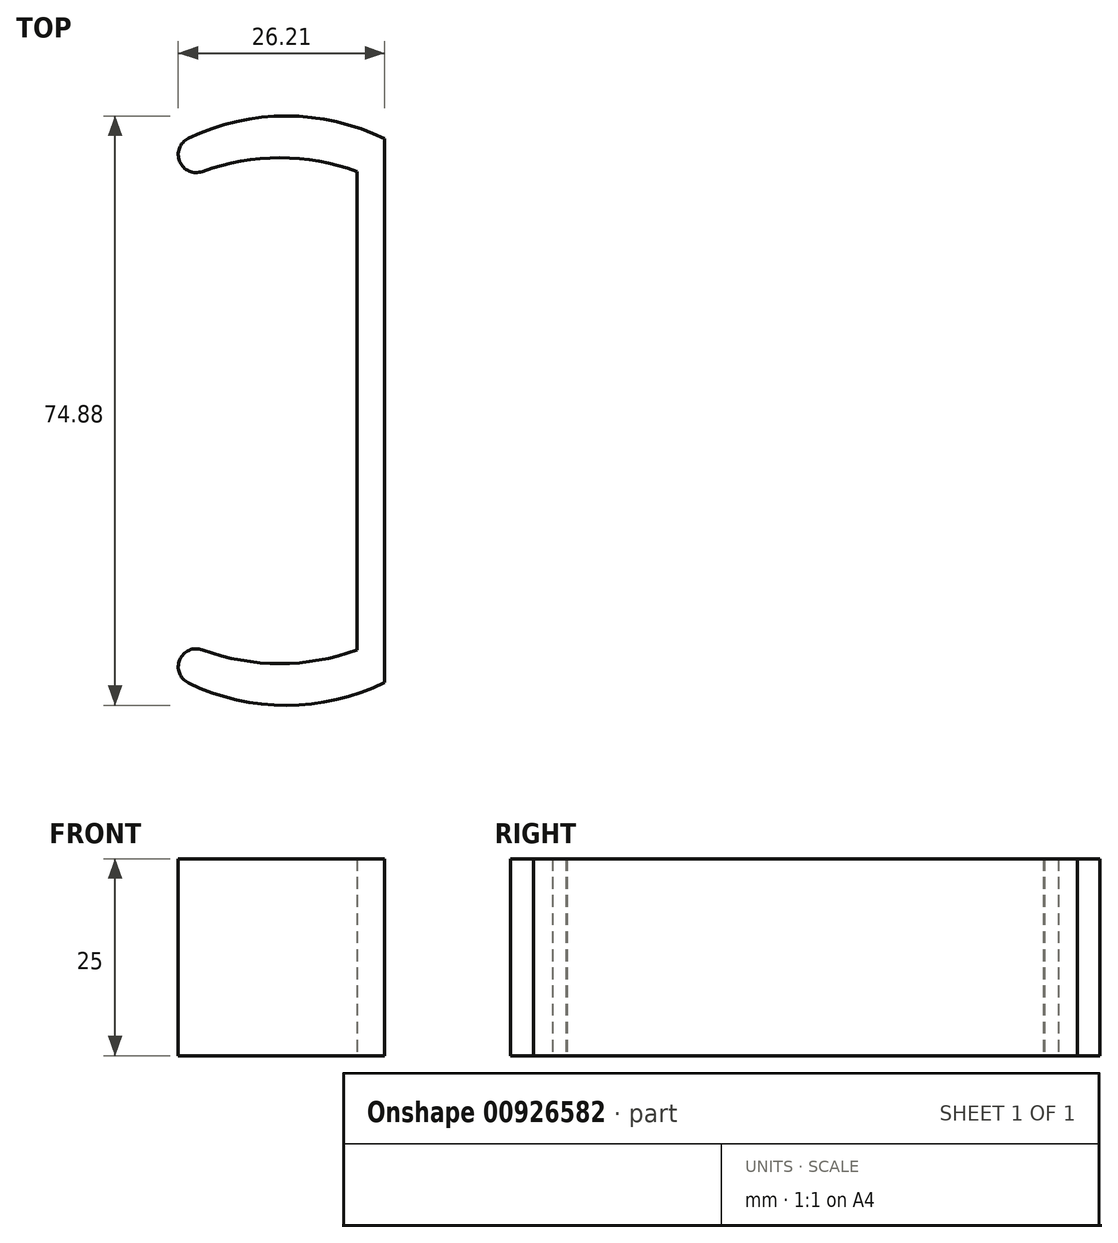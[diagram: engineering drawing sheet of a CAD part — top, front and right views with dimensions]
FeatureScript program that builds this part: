
annotation { "Feature Type Name" : "Feature", "Feature Type Description" : "" }
export const myFeature = defineFeature(function(context is Context, id is Id, definition is map)
    precondition{}
    {
        {
            var Q0;
            Q0=qCreatedBy(makeId("Top.planeOp"),FACE);
            var sketch = newSketch(context, id + "F0", { "sketchPlane" : qUnion([Q0])});
            skLineSegment(sketch, "E0", {"start": v(0, 30.4) * mm, "end": v(0, -30.4) * mm});
            skArc(sketch, "E1", {"start": v(0, 30.4) * mm, "mid": v(-9.82, 32.14) * mm, "end": v(-19.63, 30.4) * mm});
            skArc(sketch, "E2", {"start": v(3.5, 34.54) * mm, "mid": v(-8.95, 37.44) * mm, "end": v(-21.42, 34.6) * mm});
            skLineSegment(sketch, "E3", {"start": v(3.5, 34.54) * mm, "end": v(3.5, -34.54) * mm});
            skLineSegment(sketch, "E4", {"start": v(-9.7, 0) * mm, "end": v(18.93, 0) * mm, "construction": true});
            skArc(sketch, "E5.MirrorCS", {"start": v(0, -30.4) * mm, "mid": v(-9.82, -32.14) * mm, "end": v(-19.63, -30.4) * mm});
            skArc(sketch, "E6.MirrorCS", {"start": v(3.5, -34.54) * mm, "mid": v(-8.95, -37.44) * mm, "end": v(-21.42, -34.6) * mm});
            skArc(sketch, "E7", {"start": v(-21.42, 34.6) * mm, "mid": v(-22.53, 31.65) * mm, "end": v(-19.63, 30.4) * mm});
            skArc(sketch, "E8.MirrorCS", {"start": v(-21.42, -34.6) * mm, "mid": v(-22.53, -31.65) * mm, "end": v(-19.63, -30.4) * mm});
            skSolve(sketch);
        }
        {
            var Q0;
            Q0=makeQuery(id+"F0.imprint","IMPRINT",FACE,{"disambiguationData":[TD([[makeQuery(id+"F0.imprint","IMPRINT",EDGE,{"derivedFrom":sQuery(id+"F0.wireOp",EDGE,"E0")}),1.0]])]});
            extrude(context, id + "F1", {"entities" : qUnion([Q0]), "depth" : 25 * mm, "offsetDistance" : 25 * mm});
        }
    });
